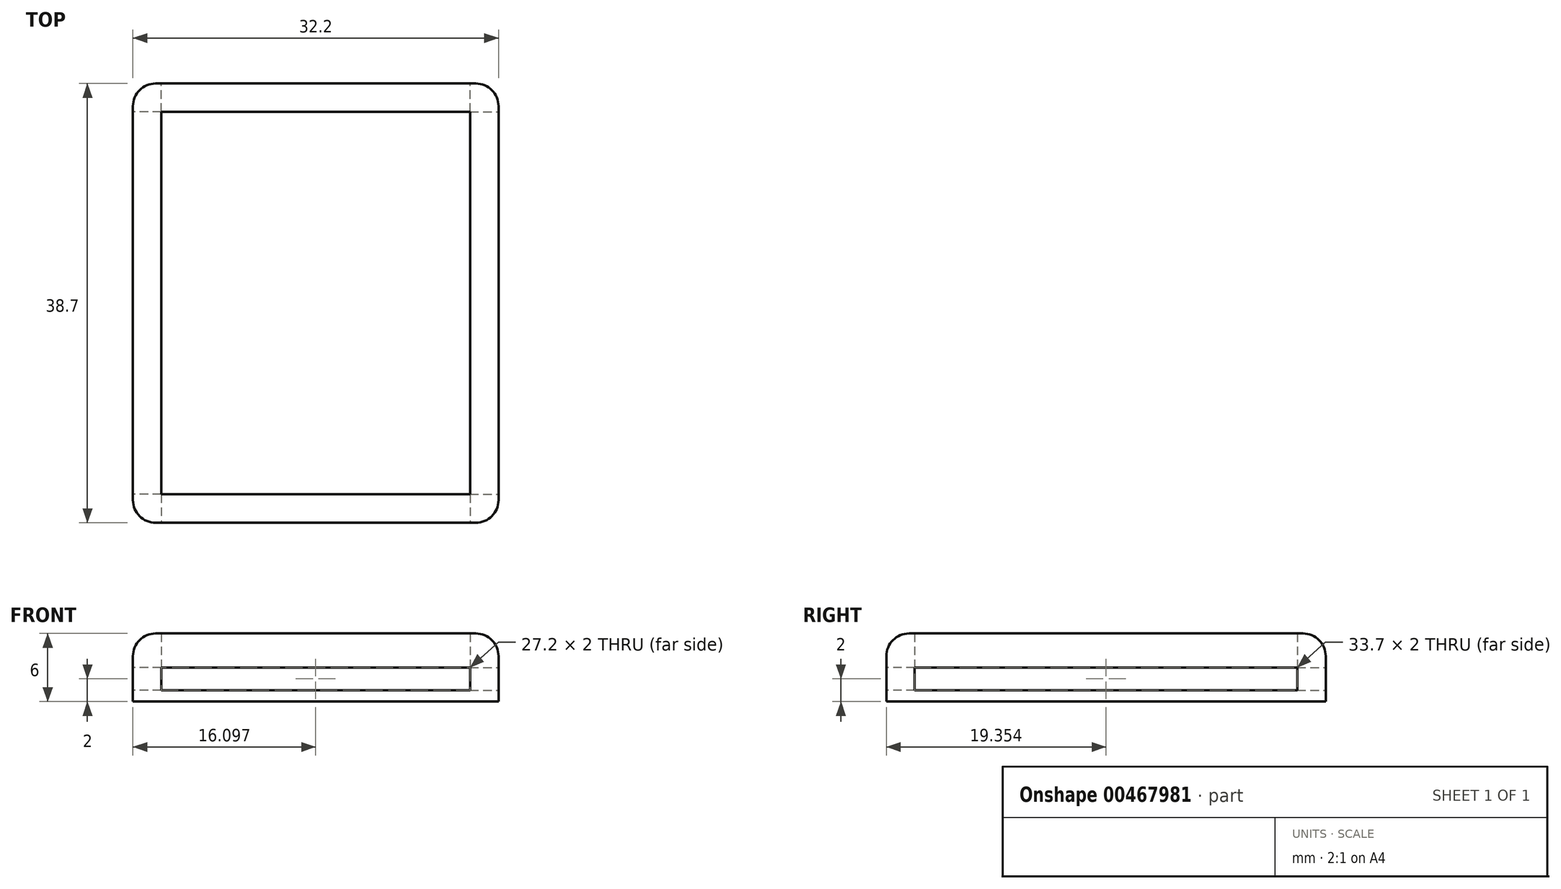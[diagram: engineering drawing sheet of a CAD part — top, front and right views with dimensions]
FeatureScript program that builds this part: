
annotation { "Feature Type Name" : "Feature", "Feature Type Description" : "" }
export const myFeature = defineFeature(function(context is Context, id is Id, definition is map)
    precondition{}
    {
        {
            var Q0;
            Q0=qCreatedBy(makeId("Top.planeOp"),FACE);
            var sketch = newSketch(context, id + "F0", { "sketchPlane" : qUnion([Q0])});
            skLineSegment(sketch, "E0.bottom", {"start": v(-13.43, 17.34) * mm, "end": v(13.77, 17.34) * mm});
            skLineSegment(sketch, "E0.top", {"start": v(-13.43, -16.36) * mm, "end": v(13.77, -16.36) * mm});
            skLineSegment(sketch, "E0.left", {"start": v(-13.43, 17.34) * mm, "end": v(-13.43, -16.36) * mm});
            skLineSegment(sketch, "E0.right", {"start": v(13.77, 17.34) * mm, "end": v(13.77, -16.36) * mm});
            skLineSegment(sketch, "E1.bottom", {"start": v(-15.93, 19.84) * mm, "end": v(16.27, 19.84) * mm});
            skLineSegment(sketch, "E1.top", {"start": v(-15.93, -18.86) * mm, "end": v(16.27, -18.86) * mm});
            skLineSegment(sketch, "E1.left", {"start": v(-15.93, 19.84) * mm, "end": v(-15.93, -18.86) * mm});
            skLineSegment(sketch, "E1.right", {"start": v(16.27, 19.84) * mm, "end": v(16.27, -18.86) * mm});
            skLineSegment(sketch, "E2.bottom", {"start": v(-13.43, -16.36) * mm, "end": v(-15.93, -16.36) * mm});
            skLineSegment(sketch, "E2.top", {"start": v(-13.43, -18.86) * mm, "end": v(-15.93, -18.86) * mm});
            skLineSegment(sketch, "E2.left", {"start": v(-13.43, -16.36) * mm, "end": v(-13.43, -18.86) * mm});
            skLineSegment(sketch, "E2.right", {"start": v(-15.93, -16.36) * mm, "end": v(-15.93, -18.86) * mm});
            skLineSegment(sketch, "E3.bottom", {"start": v(13.77, -16.36) * mm, "end": v(16.27, -16.36) * mm});
            skLineSegment(sketch, "E3.top", {"start": v(13.77, -18.86) * mm, "end": v(16.27, -18.86) * mm});
            skLineSegment(sketch, "E3.left", {"start": v(13.77, -16.36) * mm, "end": v(13.77, -18.86) * mm});
            skLineSegment(sketch, "E3.right", {"start": v(16.27, -16.36) * mm, "end": v(16.27, -18.86) * mm});
            skLineSegment(sketch, "E4.bottom", {"start": v(13.77, 17.34) * mm, "end": v(16.27, 17.34) * mm});
            skLineSegment(sketch, "E4.top", {"start": v(13.77, 19.84) * mm, "end": v(16.27, 19.84) * mm});
            skLineSegment(sketch, "E4.left", {"start": v(13.77, 17.34) * mm, "end": v(13.77, 19.84) * mm});
            skLineSegment(sketch, "E4.right", {"start": v(16.27, 17.34) * mm, "end": v(16.27, 19.84) * mm});
            skLineSegment(sketch, "E5.bottom", {"start": v(-13.43, 17.34) * mm, "end": v(-15.93, 17.34) * mm});
            skLineSegment(sketch, "E5.top", {"start": v(-13.43, 19.84) * mm, "end": v(-15.93, 19.84) * mm});
            skLineSegment(sketch, "E5.left", {"start": v(-13.43, 17.34) * mm, "end": v(-13.43, 19.84) * mm});
            skLineSegment(sketch, "E5.right", {"start": v(-15.93, 17.34) * mm, "end": v(-15.93, 19.84) * mm});
            skSolve(sketch);
        }
        {
            var Q0;
            Q0=makeQuery(id+"F0.imprint","IMPRINT",FACE,{"disambiguationData":[TD([[makeQuery(id+"F0.imprint","IMPRINT",EDGE,{"derivedFrom":sQuery(id+"F0.wireOp",EDGE,"E0.bottom")}),1.0]])]});
            var Q1;
            Q1=makeQuery(id+"F0.imprint","IMPRINT",FACE,{"disambiguationData":[TD([[makeQuery(id+"F0.imprint","IMPRINT",EDGE,{"derivedFrom":sQuery(id+"F0.wireOp",EDGE,"E0.left")}),-1.0]])]});
            var Q2;
            Q2=makeQuery(id+"F0.imprint","IMPRINT",FACE,{"disambiguationData":[TD([[makeQuery(id+"F0.imprint","IMPRINT",EDGE,{"derivedFrom":sQuery(id+"F0.wireOp",EDGE,"E5.bottom")}),-1.0]])]});
            var Q3;
            Q3=makeQuery(id+"F0.imprint","IMPRINT",FACE,{"disambiguationData":[TD([[makeQuery(id+"F0.imprint","IMPRINT",EDGE,{"derivedFrom":sQuery(id+"F0.wireOp",EDGE,"E2.bottom")}),1.0]])]});
            var Q4;
            Q4=makeQuery(id+"F0.imprint","IMPRINT",FACE,{"disambiguationData":[TD([[makeQuery(id+"F0.imprint","IMPRINT",EDGE,{"derivedFrom":sQuery(id+"F0.wireOp",EDGE,"E0.top")}),-1.0]])]});
            var Q5;
            Q5=makeQuery(id+"F0.imprint","IMPRINT",FACE,{"disambiguationData":[TD([[makeQuery(id+"F0.imprint","IMPRINT",EDGE,{"derivedFrom":sQuery(id+"F0.wireOp",EDGE,"E3.bottom")}),-1.0]])]});
            var Q6;
            Q6=makeQuery(id+"F0.imprint","IMPRINT",FACE,{"disambiguationData":[TD([[makeQuery(id+"F0.imprint","IMPRINT",EDGE,{"derivedFrom":sQuery(id+"F0.wireOp",EDGE,"E0.right")}),1.0]])]});
            var Q7;
            Q7=makeQuery(id+"F0.imprint","IMPRINT",FACE,{"disambiguationData":[TD([[makeQuery(id+"F0.imprint","IMPRINT",EDGE,{"derivedFrom":sQuery(id+"F0.wireOp",EDGE,"E4.bottom")}),1.0]])]});
            extrude(context, id + "F1", {"entities" : qUnion([Q0, Q1, Q2, Q3, Q4, Q5, Q6, Q7]), "depth" : 3 * mm});
        }
        {
            var Q0;
            Q0=makeQuery(id+"F1.opExtrude","CAP_EDGE",EDGE,{"disambiguationData":[OSD([sQuery(id+"F0.wireOp",EDGE,"E1.right")])],"isStart":false});
            var Q1;
            Q1=makeQuery(id+"F1.opExtrude","CAP_EDGE",EDGE,{"disambiguationData":[OSD([sQuery(id+"F0.wireOp",EDGE,"E1.bottom")])],"isStart":false});
            var Q2;
            Q2=makeQuery(id+"F1.opExtrude","CAP_EDGE",EDGE,{"disambiguationData":[OSD([sQuery(id+"F0.wireOp",EDGE,"E1.left")])],"isStart":false});
            var Q3;
            Q3=makeQuery(id+"F1.opExtrude","CAP_EDGE",EDGE,{"disambiguationData":[OSD([sQuery(id+"F0.wireOp",EDGE,"E1.top")])],"isStart":false});
            fillet(context, id + "F2", {"entities" : qUnion([Q0, Q1, Q2, Q3]), "radius" : 2 * mm, "tangentPropagation" : true, "allowEdgeOverflow" : false});
        }
        {
            var Q0;
            Q0=makeQuery(id+"F0.imprint","IMPRINT",FACE,{"disambiguationData":[TD([[makeQuery(id+"F0.imprint","IMPRINT",EDGE,{"derivedFrom":sQuery(id+"F0.wireOp",EDGE,"E2.bottom")}),1.0]])]});
            var Q1;
            Q1=makeQuery(id+"F0.imprint","IMPRINT",FACE,{"disambiguationData":[TD([[makeQuery(id+"F0.imprint","IMPRINT",EDGE,{"derivedFrom":sQuery(id+"F0.wireOp",EDGE,"E3.bottom")}),-1.0]])]});
            var Q2;
            Q2=makeQuery(id+"F0.imprint","IMPRINT",FACE,{"disambiguationData":[TD([[makeQuery(id+"F0.imprint","IMPRINT",EDGE,{"derivedFrom":sQuery(id+"F0.wireOp",EDGE,"E4.bottom")}),1.0]])]});
            var Q3;
            Q3=makeQuery(id+"F0.imprint","IMPRINT",FACE,{"disambiguationData":[TD([[makeQuery(id+"F0.imprint","IMPRINT",EDGE,{"derivedFrom":sQuery(id+"F0.wireOp",EDGE,"E5.bottom")}),-1.0]])]});
            extrude(context, id + "F3", {"entities" : qUnion([Q0, Q1, Q2, Q3]), "operationType" : NewBodyOperationType.ADD, "oppositeDirection" : true, "depth" : 2 * mm});
        }
        {
            var Q0;
            Q0=makeQuery(id+"F3.opExtrude","CAP_FACE",FACE,{"disambiguationData":[OSD([sQuery(id+"F0.wireOp",EDGE,"E5.bottom"),sQuery(id+"F0.wireOp",EDGE,"E5.top"),sQuery(id+"F0.wireOp",EDGE,"E5.left"),sQuery(id+"F0.wireOp",EDGE,"E5.right")])],"isStart":false});
            var sketch = newSketch(context, id + "F4", { "sketchPlane" : qUnion([Q0])});
            skPoint(sketch, "E6.0", {"position": v(16.27, -19.84) * mm});
            skPoint(sketch, "E7.0", {"position": v(-15.93, 18.86) * mm});
            skLineSegment(sketch, "E8.bottom", {"start": v(16.27, -19.84) * mm, "end": v(-15.93, -19.84) * mm});
            skLineSegment(sketch, "E8.top", {"start": v(16.27, 18.86) * mm, "end": v(-15.93, 18.86) * mm});
            skLineSegment(sketch, "E8.left", {"start": v(16.27, -19.84) * mm, "end": v(16.27, 18.86) * mm});
            skLineSegment(sketch, "E8.right", {"start": v(-15.93, -19.84) * mm, "end": v(-15.93, 18.86) * mm});
            skSolve(sketch);
        }
        {
            var Q0;
            {var subQ2=sQuery(id+"F4.wireOp",EDGE,"E8.top");Q0=makeQuery(id+"F4.imprint","IMPRINT",FACE,{"disambiguationData":[TD([[makeQuery(id+"F4.imprint","IMPRINT",EDGE,{"derivedFrom":subQ2}),1.0]])]});}
            var Q1;
            {var subQ4=makeQuery(id+"F3.opExtrude","CAP_EDGE",EDGE,{"disambiguationData":[OSD([sQuery(id+"F0.wireOp",EDGE,"E5.bottom")])],"isStart":false});Q1=makeQuery(id+"F4.imprint","IMPRINT",FACE,{"disambiguationData":[TD([[makeQuery(id+"F4.imprint","IMPRINT",EDGE,{"derivedFrom":subQ4}),1.0]])]});}
            extrude(context, id + "F5", {"entities" : qUnion([Q0, Q1]), "operationType" : NewBodyOperationType.ADD, "depth" : 1 * mm});
        }
        {
            var Q0;
            {var subQ0=sQuery(id+"F0.wireOp",EDGE,"E4.right");var subQ1=sQuery(id+"F0.wireOp",EDGE,"E4.top");Q0=makeQuery(id+"F5.boolean.opBoolean","MERGE",EDGE,{"derivedFrom":[makeQuery(id+"F3.boolean.opBoolean","MERGE",EDGE,{"derivedFrom":[makeQuery(id+"F1.opExtrude","SWEPT_EDGE",EDGE,{"disambiguationData":[OSD([subQ1,subQ0])]}),makeQuery(id+"F3.opExtrude","SWEPT_EDGE",EDGE,{"disambiguationData":[OSD([subQ1,subQ0])]})]}),makeQuery(id+"F5.opExtrude","SWEPT_EDGE",EDGE,{"disambiguationData":[OSD([sQuery(id+"F4.wireOp",EDGE,"E8.bottom"),sQuery(id+"F4.wireOp",EDGE,"E8.left")])]})]});}
            var Q1;
            {var subQ0=sQuery(id+"F0.wireOp",EDGE,"E3.right");var subQ1=sQuery(id+"F0.wireOp",EDGE,"E3.top");Q1=makeQuery(id+"F5.boolean.opBoolean","MERGE",EDGE,{"derivedFrom":[makeQuery(id+"F3.boolean.opBoolean","MERGE",EDGE,{"derivedFrom":[makeQuery(id+"F1.opExtrude","SWEPT_EDGE",EDGE,{"disambiguationData":[OSD([subQ1,subQ0])]}),makeQuery(id+"F3.opExtrude","SWEPT_EDGE",EDGE,{"disambiguationData":[OSD([subQ1,subQ0])]})]}),makeQuery(id+"F5.opExtrude","SWEPT_EDGE",EDGE,{"disambiguationData":[OSD([sQuery(id+"F4.wireOp",EDGE,"E8.top"),sQuery(id+"F4.wireOp",EDGE,"E8.left")])]})]});}
            var Q2;
            {var subQ0=sQuery(id+"F0.wireOp",EDGE,"E2.right");var subQ1=sQuery(id+"F0.wireOp",EDGE,"E2.top");Q2=makeQuery(id+"F5.boolean.opBoolean","MERGE",EDGE,{"derivedFrom":[makeQuery(id+"F3.boolean.opBoolean","MERGE",EDGE,{"derivedFrom":[makeQuery(id+"F1.opExtrude","SWEPT_EDGE",EDGE,{"disambiguationData":[OSD([subQ1,subQ0])]}),makeQuery(id+"F3.opExtrude","SWEPT_EDGE",EDGE,{"disambiguationData":[OSD([subQ1,subQ0])]})]}),makeQuery(id+"F5.opExtrude","SWEPT_EDGE",EDGE,{"disambiguationData":[OSD([sQuery(id+"F4.wireOp",EDGE,"E8.top"),sQuery(id+"F4.wireOp",EDGE,"E8.right")])]})]});}
            var Q3;
            {var subQ0=sQuery(id+"F0.wireOp",EDGE,"E5.right");var subQ1=sQuery(id+"F0.wireOp",EDGE,"E5.top");Q3=makeQuery(id+"F5.boolean.opBoolean","MERGE",EDGE,{"derivedFrom":[makeQuery(id+"F3.boolean.opBoolean","MERGE",EDGE,{"derivedFrom":[makeQuery(id+"F1.opExtrude","SWEPT_EDGE",EDGE,{"disambiguationData":[OSD([subQ1,subQ0])]}),makeQuery(id+"F3.opExtrude","SWEPT_EDGE",EDGE,{"disambiguationData":[OSD([subQ1,subQ0])]})]}),makeQuery(id+"F5.opExtrude","SWEPT_EDGE",EDGE,{"disambiguationData":[OSD([sQuery(id+"F4.wireOp",EDGE,"E8.bottom"),sQuery(id+"F4.wireOp",EDGE,"E8.right")])]})]});}
            fillet(context, id + "F6", {"entities" : qUnion([Q0, Q1, Q2, Q3]), "radius" : 2 * mm, "tangentPropagation" : true, "allowEdgeOverflow" : false});
        }
    });
